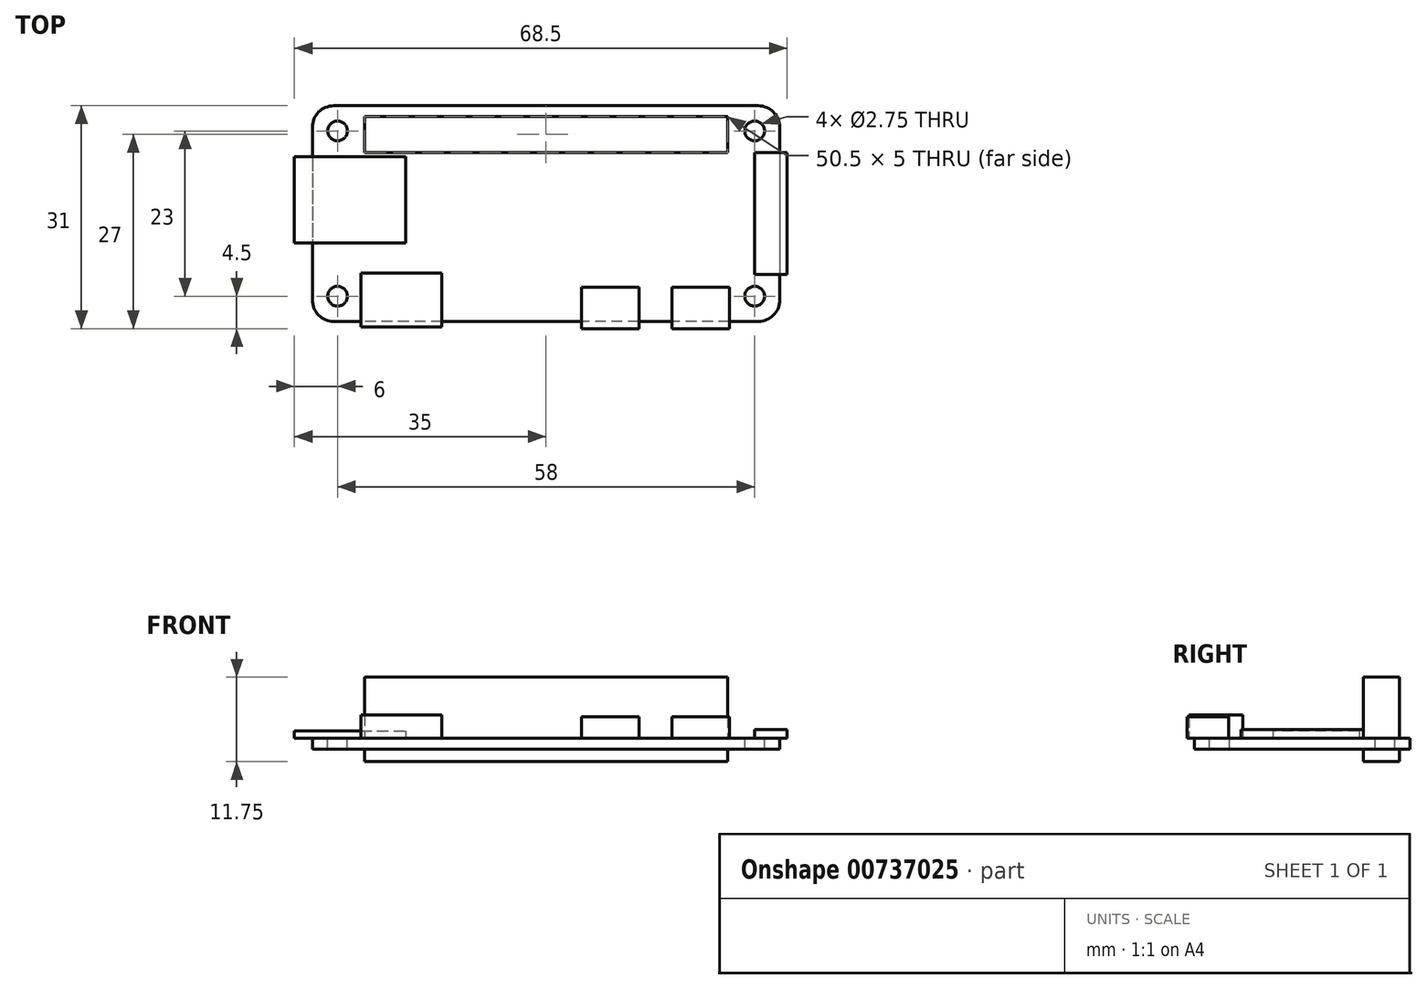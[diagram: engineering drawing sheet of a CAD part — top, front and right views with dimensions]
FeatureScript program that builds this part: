
annotation { "Feature Type Name" : "Feature", "Feature Type Description" : "" }
export const myFeature = defineFeature(function(context is Context, id is Id, definition is map)
    precondition{}
    {
        {
            var Q0;
            Q0=qCreatedBy(makeId("Top.planeOp"),FACE);
            var sketch = newSketch(context, id + "F0", { "sketchPlane" : qUnion([Q0])});
            skLineSegment(sketch, "E0.bottom", {"start": v(29.5, 15) * mm, "end": v(-29.5, 15) * mm});
            skLineSegment(sketch, "E0.top", {"start": v(29.5, -15) * mm, "end": v(-29.5, -15) * mm});
            skLineSegment(sketch, "E0.left", {"start": v(32.5, 12) * mm, "end": v(32.5, -12) * mm});
            skLineSegment(sketch, "E0.right", {"start": v(-32.5, 12) * mm, "end": v(-32.5, -12) * mm});
            skPoint(sketch, "E0.middle", {"position": v(0, 0) * mm});
            skCircle(sketch, "E1", {"center": v(29, 11.5) * mm, "radius": 1.38 * mm});
            skCircle(sketch, "E2", {"center": v(29, -11.5) * mm, "radius": 1.38 * mm});
            skCircle(sketch, "E3", {"center": v(-29, -11.5) * mm, "radius": 1.38 * mm});
            skCircle(sketch, "E4", {"center": v(-29, 11.5) * mm, "radius": 1.38 * mm});
            skPoint(sketch, "E5.visualSharp", {"position": v(32.5, 15) * mm});
            skArc(sketch, "E5.filletArc", {"start": v(32.5, 12) * mm, "mid": v(31.62, 14.12) * mm, "end": v(29.5, 15) * mm});
            skPoint(sketch, "E6.visualSharp", {"position": v(32.5, -15) * mm});
            skArc(sketch, "E6.filletArc", {"start": v(29.5, -15) * mm, "mid": v(31.62, -14.12) * mm, "end": v(32.5, -12) * mm});
            skPoint(sketch, "E7.visualSharp", {"position": v(-32.5, -15) * mm});
            skArc(sketch, "E7.filletArc", {"start": v(-32.5, -12) * mm, "mid": v(-31.62, -14.12) * mm, "end": v(-29.5, -15) * mm});
            skPoint(sketch, "E8.visualSharp", {"position": v(-32.5, 15) * mm});
            skArc(sketch, "E8.filletArc", {"start": v(-29.5, 15) * mm, "mid": v(-31.62, 14.12) * mm, "end": v(-32.5, 12) * mm});
            skLineSegment(sketch, "E9.bottom", {"start": v(-14.47, -8.25) * mm, "end": v(-25.72, -8.25) * mm});
            skLineSegment(sketch, "E9.top", {"start": v(-14.47, -15.75) * mm, "end": v(-25.72, -15.75) * mm});
            skLineSegment(sketch, "E9.left", {"start": v(-14.47, -8.25) * mm, "end": v(-14.47, -15.75) * mm});
            skLineSegment(sketch, "E9.right", {"start": v(-25.72, -8.25) * mm, "end": v(-25.72, -15.75) * mm});
            skPoint(sketch, "E9.middle", {"position": v(-20.1, -12) * mm});
            skLineSegment(sketch, "E10.bottom", {"start": v(12.9, -10.25) * mm, "end": v(4.9, -10.25) * mm});
            skLineSegment(sketch, "E10.top", {"start": v(12.9, -16) * mm, "end": v(4.9, -16) * mm});
            skLineSegment(sketch, "E10.left", {"start": v(12.9, -10.25) * mm, "end": v(12.9, -16) * mm});
            skLineSegment(sketch, "E10.right", {"start": v(4.9, -10.25) * mm, "end": v(4.9, -16) * mm});
            skPoint(sketch, "E10.middle", {"position": v(8.9, -13.13) * mm});
            skLineSegment(sketch, "E11.bottom", {"start": v(25.5, -10.25) * mm, "end": v(17.5, -10.25) * mm});
            skLineSegment(sketch, "E11.top", {"start": v(25.5, -16) * mm, "end": v(17.5, -16) * mm});
            skLineSegment(sketch, "E11.left", {"start": v(25.5, -10.25) * mm, "end": v(25.5, -16) * mm});
            skLineSegment(sketch, "E11.right", {"start": v(17.5, -10.25) * mm, "end": v(17.5, -16) * mm});
            skPoint(sketch, "E11.middle", {"position": v(21.5, -13.12) * mm});
            skLineSegment(sketch, "E12.bottom", {"start": v(-35, 7.9) * mm, "end": v(-19.5, 7.9) * mm});
            skLineSegment(sketch, "E12.top", {"start": v(-35, -4.1) * mm, "end": v(-19.5, -4.1) * mm});
            skLineSegment(sketch, "E12.left", {"start": v(-35, 7.9) * mm, "end": v(-35, -4.1) * mm});
            skLineSegment(sketch, "E12.right", {"start": v(-19.5, 7.9) * mm, "end": v(-19.5, -4.1) * mm});
            skPoint(sketch, "E12.middle", {"position": v(-27.25, 1.9) * mm});
            skLineSegment(sketch, "E13.bottom", {"start": v(33.5, -8.5) * mm, "end": v(29, -8.5) * mm});
            skLineSegment(sketch, "E13.top", {"start": v(33.5, 8.5) * mm, "end": v(29, 8.5) * mm});
            skLineSegment(sketch, "E13.left", {"start": v(33.5, -8.5) * mm, "end": v(33.5, 8.5) * mm});
            skLineSegment(sketch, "E13.right", {"start": v(29, -8.5) * mm, "end": v(29, 8.5) * mm});
            skPoint(sketch, "E13.middle", {"position": v(31.25, 0) * mm});
            skLineSegment(sketch, "E14.bottom", {"start": v(25.25, 8.5) * mm, "end": v(-25.25, 8.5) * mm});
            skLineSegment(sketch, "E14.top", {"start": v(25.25, 13.5) * mm, "end": v(-25.25, 13.5) * mm});
            skLineSegment(sketch, "E14.left", {"start": v(25.25, 8.5) * mm, "end": v(25.25, 13.5) * mm});
            skLineSegment(sketch, "E14.right", {"start": v(-25.25, 8.5) * mm, "end": v(-25.25, 13.5) * mm});
            skPoint(sketch, "E14.middle", {"position": v(0, 11) * mm});
            skSolve(sketch);
        }
        {
            var Q0;
            {var subQ5=sQuery(id+"F0.wireOp",EDGE,"E11.bottom");Q0=makeQuery(id+"F0.imprint","IMPRINT",FACE,{"disambiguationData":[TD([[makeQuery(id+"F0.imprint","IMPRINT",EDGE,{"derivedFrom":subQ5}),1.0]])]});}
            var Q1;
            {var subQ5=sQuery(id+"F0.wireOp",EDGE,"E10.bottom");Q1=makeQuery(id+"F0.imprint","IMPRINT",FACE,{"disambiguationData":[TD([[makeQuery(id+"F0.imprint","IMPRINT",EDGE,{"derivedFrom":subQ5}),1.0]])]});}
            var Q2;
            {var subQ5=sQuery(id+"F0.wireOp",EDGE,"E9.bottom");Q2=makeQuery(id+"F0.imprint","IMPRINT",FACE,{"disambiguationData":[TD([[makeQuery(id+"F0.imprint","IMPRINT",EDGE,{"derivedFrom":subQ5}),1.0]])]});}
            var Q3;
            {var subQ5=sQuery(id+"F0.wireOp",EDGE,"E13.right");Q3=makeQuery(id+"F0.imprint","IMPRINT",FACE,{"disambiguationData":[TD([[makeQuery(id+"F0.imprint","IMPRINT",EDGE,{"derivedFrom":subQ5}),-1.0]])]});}
            var Q4;
            {var subQ5=sQuery(id+"F0.wireOp",EDGE,"E12.right");Q4=makeQuery(id+"F0.imprint","IMPRINT",FACE,{"disambiguationData":[TD([[makeQuery(id+"F0.imprint","IMPRINT",EDGE,{"derivedFrom":subQ5}),-1.0]])]});}
            var Q5;
            Q5=makeQuery(id+"F0.imprint","IMPRINT",FACE,{"disambiguationData":[TD([[makeQuery(id+"F0.imprint","IMPRINT",EDGE,{"derivedFrom":sQuery(id+"F0.wireOp",EDGE,"E0.bottom")}),1.0]])]});
            var Q6;
            Q6=makeQuery(id+"F0.imprint","IMPRINT",FACE,{"disambiguationData":[TD([[makeQuery(id+"F0.imprint","IMPRINT",EDGE,{"derivedFrom":sQuery(id+"F0.wireOp",EDGE,"E14.bottom")}),-1.0]])]});
            extrude(context, id + "F1", {"entities" : qUnion([Q0, Q1, Q2, Q3, Q4, Q5, Q6]), "oppositeDirection" : true, "depth" : 1.5 * mm, "offsetDistance" : 25 * mm});
        }
        {
            var Q0;
            Q0=makeQuery(id+"F0.imprint","IMPRINT",FACE,{"disambiguationData":[TD([[makeQuery(id+"F0.imprint","IMPRINT",EDGE,{"derivedFrom":sQuery(id+"F0.wireOp",EDGE,"E14.bottom")}),-1.0]])]});
            extrude(context, id + "F2", {"entities" : qUnion([Q0]), "operationType" : NewBodyOperationType.ADD, "oppositeDirection" : true, "depth" : 3.25 * mm, "offsetDistance" : 25 * mm});
        }
        {
            var Q0;
            {var subQ5=sQuery(id+"F0.wireOp",EDGE,"E12.left");Q0=makeQuery(id+"F0.imprint","IMPRINT",FACE,{"disambiguationData":[TD([[makeQuery(id+"F0.imprint","IMPRINT",EDGE,{"derivedFrom":subQ5}),1.0]])]});}
            var Q1;
            {var subQ5=sQuery(id+"F0.wireOp",EDGE,"E12.right");Q1=makeQuery(id+"F0.imprint","IMPRINT",FACE,{"disambiguationData":[TD([[makeQuery(id+"F0.imprint","IMPRINT",EDGE,{"derivedFrom":subQ5}),-1.0]])]});}
            extrude(context, id + "F3", {"entities" : qUnion([Q0, Q1]), "operationType" : NewBodyOperationType.ADD, "depth" : 1 * mm, "offsetDistance" : 25 * mm});
        }
        {
            var Q0;
            {var subQ5=sQuery(id+"F0.wireOp",EDGE,"E9.bottom");Q0=makeQuery(id+"F0.imprint","IMPRINT",FACE,{"disambiguationData":[TD([[makeQuery(id+"F0.imprint","IMPRINT",EDGE,{"derivedFrom":subQ5}),1.0]])]});}
            var Q1;
            {var subQ5=sQuery(id+"F0.wireOp",EDGE,"E9.top");Q1=makeQuery(id+"F0.imprint","IMPRINT",FACE,{"disambiguationData":[TD([[makeQuery(id+"F0.imprint","IMPRINT",EDGE,{"derivedFrom":subQ5}),-1.0]])]});}
            extrude(context, id + "F4", {"entities" : qUnion([Q0, Q1]), "operationType" : NewBodyOperationType.ADD, "depth" : 3.25 * mm, "offsetDistance" : 25 * mm});
        }
        {
            var Q0;
            {var subQ5=sQuery(id+"F0.wireOp",EDGE,"E10.bottom");Q0=makeQuery(id+"F0.imprint","IMPRINT",FACE,{"disambiguationData":[TD([[makeQuery(id+"F0.imprint","IMPRINT",EDGE,{"derivedFrom":subQ5}),1.0]])]});}
            var Q1;
            {var subQ5=sQuery(id+"F0.wireOp",EDGE,"E11.bottom");Q1=makeQuery(id+"F0.imprint","IMPRINT",FACE,{"disambiguationData":[TD([[makeQuery(id+"F0.imprint","IMPRINT",EDGE,{"derivedFrom":subQ5}),1.0]])]});}
            var Q2;
            {var subQ5=sQuery(id+"F0.wireOp",EDGE,"E11.top");Q2=makeQuery(id+"F0.imprint","IMPRINT",FACE,{"disambiguationData":[TD([[makeQuery(id+"F0.imprint","IMPRINT",EDGE,{"derivedFrom":subQ5}),-1.0]])]});}
            var Q3;
            {var subQ5=sQuery(id+"F0.wireOp",EDGE,"E10.top");Q3=makeQuery(id+"F0.imprint","IMPRINT",FACE,{"disambiguationData":[TD([[makeQuery(id+"F0.imprint","IMPRINT",EDGE,{"derivedFrom":subQ5}),-1.0]])]});}
            extrude(context, id + "F5", {"entities" : qUnion([Q0, Q1, Q2, Q3]), "operationType" : NewBodyOperationType.ADD, "depth" : 3 * mm, "offsetDistance" : 25 * mm});
        }
        {
            var Q0;
            {var subQ5=sQuery(id+"F0.wireOp",EDGE,"E13.right");Q0=makeQuery(id+"F0.imprint","IMPRINT",FACE,{"disambiguationData":[TD([[makeQuery(id+"F0.imprint","IMPRINT",EDGE,{"derivedFrom":subQ5}),-1.0]])]});}
            var Q1;
            {var subQ5=sQuery(id+"F0.wireOp",EDGE,"E13.left");Q1=makeQuery(id+"F0.imprint","IMPRINT",FACE,{"disambiguationData":[TD([[makeQuery(id+"F0.imprint","IMPRINT",EDGE,{"derivedFrom":subQ5}),1.0]])]});}
            extrude(context, id + "F6", {"entities" : qUnion([Q0, Q1]), "operationType" : NewBodyOperationType.ADD, "depth" : 1.25 * mm, "offsetDistance" : 25 * mm});
        }
        {
            var Q0;
            Q0=makeQuery(id+"F0.imprint","IMPRINT",FACE,{"disambiguationData":[TD([[makeQuery(id+"F0.imprint","IMPRINT",EDGE,{"derivedFrom":sQuery(id+"F0.wireOp",EDGE,"E14.bottom")}),-1.0]])]});
            extrude(context, id + "F7", {"entities" : qUnion([Q0]), "operationType" : NewBodyOperationType.ADD, "depth" : 8.5 * mm, "offsetDistance" : 25 * mm});
        }
    });
